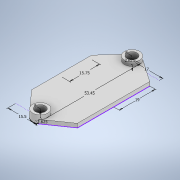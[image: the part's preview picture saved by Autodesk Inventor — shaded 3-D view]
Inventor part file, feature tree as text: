
AUTODESK INVENTOR PART (.ipt)
format: ipt  version: 2020 (Build 240168000, 168)  size: 126,976 bytes
history: native  units: in
note: dims shown in document units (in); Inventor stores cm internally (conversion verified against a paired STEP export)
features: extrude x2, sketch x1
ambient origin geometry x8: Origin, YZ Plane, XZ Plane, XY Plane, X Axis, Y Axis, Z Axis, Center Point
bodies: Solid1 (feature_tree)
feature tree (3):
  sketch  "Sketch1"  dims[d0=2.1043in d1=0.1033in d2=0.1033in d3=0.315in d4=0.315in d5=0.6102in d6=0.6201in d7=0.6693in d8=0.748in d9=0.0787in d10=0.0in d11=0.1575in d12=0.0in]
  extrude  "Extrusion1"  Depth=0.1033in
  extrude  "Extrusion2"  Depth=0.1033in
